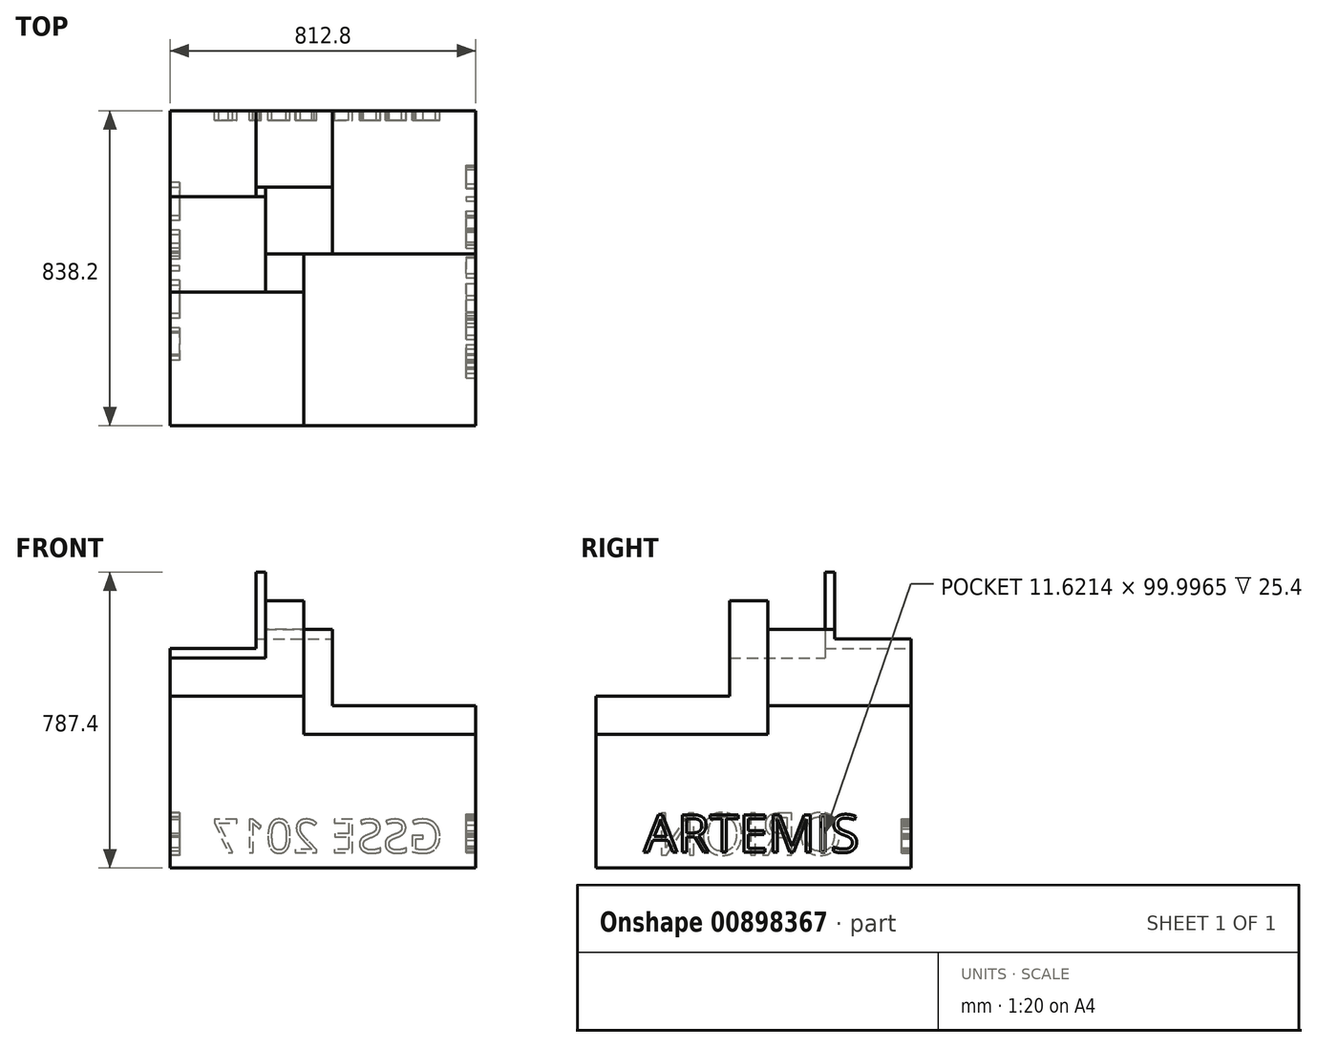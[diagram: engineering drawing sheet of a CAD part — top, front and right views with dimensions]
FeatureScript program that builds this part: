
annotation { "Feature Type Name" : "Feature", "Feature Type Description" : "" }
export const myFeature = defineFeature(function(context is Context, id is Id, definition is map)
    precondition{}
    {
        {
            var Q0;
            Q0=qCreatedBy(makeId("Top.planeOp"),FACE);
            var sketch = newSketch(context, id + "F0", { "sketchPlane" : qUnion([Q0])});
            skLineSegment(sketch, "E0.bottom", {"start": v(-76.2, -68.1) * mm, "end": v(381, -68.1) * mm});
            skLineSegment(sketch, "E0.top", {"start": v(-76.2, -525.3) * mm, "end": v(381, -525.3) * mm});
            skLineSegment(sketch, "E0.left", {"start": v(-76.2, -68.1) * mm, "end": v(-76.2, -525.3) * mm});
            skLineSegment(sketch, "E0.right", {"start": v(381, -68.1) * mm, "end": v(381, -525.3) * mm});
            skLineSegment(sketch, "E1.bottom", {"start": v(-76.2, -525.3) * mm, "end": v(-431.8, -525.3) * mm});
            skLineSegment(sketch, "E1.top", {"start": v(-76.2, -169.7) * mm, "end": v(-431.8, -169.7) * mm});
            skLineSegment(sketch, "E1.left", {"start": v(-76.2, -525.3) * mm, "end": v(-76.2, -169.7) * mm});
            skLineSegment(sketch, "E1.right", {"start": v(-431.8, -525.3) * mm, "end": v(-431.8, -169.7) * mm});
            skLineSegment(sketch, "E2.bottom", {"start": v(-76.2, -169.7) * mm, "end": v(-177.8, -169.7) * mm});
            skLineSegment(sketch, "E2.top", {"start": v(-76.2, -68.1) * mm, "end": v(-177.8, -68.1) * mm});
            skLineSegment(sketch, "E2.left", {"start": v(-76.2, -169.7) * mm, "end": v(-76.2, -68.1) * mm});
            skLineSegment(sketch, "E2.right", {"start": v(-177.8, -169.7) * mm, "end": v(-177.8, -68.1) * mm});
            skLineSegment(sketch, "E3.bottom", {"start": v(-431.8, -169.7) * mm, "end": v(-177.8, -169.7) * mm});
            skLineSegment(sketch, "E3.top", {"start": v(-431.8, 84.3) * mm, "end": v(-177.8, 84.3) * mm});
            skLineSegment(sketch, "E3.left", {"start": v(-431.8, -169.7) * mm, "end": v(-431.8, 84.3) * mm});
            skLineSegment(sketch, "E3.right", {"start": v(-177.8, -169.7) * mm, "end": v(-177.8, 84.3) * mm});
            skLineSegment(sketch, "E4.bottom", {"start": v(-431.8, 84.3) * mm, "end": v(-203.2, 84.3) * mm});
            skLineSegment(sketch, "E4.top", {"start": v(-431.8, 312.9) * mm, "end": v(-203.2, 312.9) * mm});
            skLineSegment(sketch, "E4.left", {"start": v(-431.8, 84.3) * mm, "end": v(-431.8, 312.9) * mm});
            skLineSegment(sketch, "E4.right", {"start": v(-203.2, 84.3) * mm, "end": v(-203.2, 312.9) * mm});
            skLineSegment(sketch, "E5.bottom", {"start": v(381, -68.1) * mm, "end": v(0, -68.1) * mm});
            skLineSegment(sketch, "E5.top", {"start": v(381, 312.9) * mm, "end": v(0, 312.9) * mm});
            skLineSegment(sketch, "E5.left", {"start": v(381, -68.1) * mm, "end": v(381, 312.9) * mm});
            skLineSegment(sketch, "E5.right", {"start": v(0, -68.1) * mm, "end": v(0, 312.9) * mm});
            skLineSegment(sketch, "E6.bottom", {"start": v(-203.2, 312.9) * mm, "end": v(0, 312.9) * mm});
            skLineSegment(sketch, "E6.top", {"start": v(-203.2, 109.7) * mm, "end": v(0, 109.7) * mm});
            skLineSegment(sketch, "E6.left", {"start": v(-203.2, 312.9) * mm, "end": v(-203.2, 109.7) * mm});
            skLineSegment(sketch, "E6.right", {"start": v(0, 312.9) * mm, "end": v(0, 109.7) * mm});
            skLineSegment(sketch, "E7.bottom", {"start": v(0, -68.1) * mm, "end": v(-177.8, -68.1) * mm});
            skLineSegment(sketch, "E7.top", {"start": v(0, 109.7) * mm, "end": v(-177.8, 109.7) * mm});
            skLineSegment(sketch, "E7.left", {"start": v(0, -68.1) * mm, "end": v(0, 109.7) * mm});
            skLineSegment(sketch, "E7.right", {"start": v(-177.8, -68.1) * mm, "end": v(-177.8, 109.7) * mm});
            skSolve(sketch);
        }
        {
            var Q0;
            {var subQ0=sQuery(id+"F0.wireOp",EDGE,"E7.right");Q0=makeQuery(id+"F0.imprint","IMPRINT",FACE,{"disambiguationData":[TD([[makeQuery(id+"F0.imprint","IMPRINT",EDGE,{"derivedFrom":subQ0}),1.0]])]});}
            extrude(context, id + "F1", {"entities" : qUnion([Q0]), "depth" : 787.4 * mm, "offsetDistance" : 25.4 * mm});
        }
        {
            var Q0;
            {var subQ1=sQuery(id+"F0.wireOp",EDGE,"E4.top");Q0=makeQuery(id+"F0.imprint","IMPRINT",FACE,{"disambiguationData":[TD([[makeQuery(id+"F0.imprint","IMPRINT",EDGE,{"derivedFrom":subQ1}),-1.0]])]});}
            extrude(context, id + "F2", {"entities" : qUnion([Q0]), "operationType" : NewBodyOperationType.ADD, "depth" : 584.2 * mm, "offsetDistance" : 25.4 * mm});
        }
        {
            var Q0;
            {var subQ4=sQuery(id+"F0.wireOp",EDGE,"E6.bottom");Q0=makeQuery(id+"F0.imprint","IMPRINT",FACE,{"disambiguationData":[TD([[makeQuery(id+"F0.imprint","IMPRINT",EDGE,{"derivedFrom":subQ4}),-1.0]])]});}
            extrude(context, id + "F3", {"entities" : qUnion([Q0]), "operationType" : NewBodyOperationType.ADD, "depth" : 609.6 * mm, "offsetDistance" : 25.4 * mm});
        }
        {
            var Q0;
            {var subQ1=sQuery(id+"F0.wireOp",EDGE,"E5.top");Q0=makeQuery(id+"F0.imprint","IMPRINT",FACE,{"disambiguationData":[TD([[makeQuery(id+"F0.imprint","IMPRINT",EDGE,{"derivedFrom":subQ1}),1.0]])]});}
            extrude(context, id + "F4", {"entities" : qUnion([Q0]), "operationType" : NewBodyOperationType.ADD, "depth" : 431.8 * mm, "offsetDistance" : 25.4 * mm});
        }
        {
            var Q0;
            {var subQ5=sQuery(id+"F0.wireOp",EDGE,"E2.top");Q0=makeQuery(id+"F0.imprint","IMPRINT",FACE,{"disambiguationData":[TD([[makeQuery(id+"F0.imprint","IMPRINT",EDGE,{"derivedFrom":subQ5}),-1.0]])]});}
            extrude(context, id + "F5", {"entities" : qUnion([Q0]), "operationType" : NewBodyOperationType.ADD, "depth" : 635 * mm, "offsetDistance" : 25.4 * mm});
        }
        {
            var Q0;
            {var subQ3=sQuery(id+"F0.wireOp",EDGE,"E2.right");Q0=makeQuery(id+"F0.imprint","IMPRINT",FACE,{"disambiguationData":[TD([[makeQuery(id+"F0.imprint","IMPRINT",EDGE,{"derivedFrom":subQ3}),1.0]])]});}
            extrude(context, id + "F6", {"entities" : qUnion([Q0]), "operationType" : NewBodyOperationType.ADD, "depth" : 558.8 * mm, "offsetDistance" : 25.4 * mm});
        }
        {
            var Q0;
            {var subQ3=sQuery(id+"F0.wireOp",EDGE,"E2.top");Q0=makeQuery(id+"F0.imprint","IMPRINT",FACE,{"disambiguationData":[TD([[makeQuery(id+"F0.imprint","IMPRINT",EDGE,{"derivedFrom":subQ3}),1.0]])]});}
            extrude(context, id + "F7", {"entities" : qUnion([Q0]), "operationType" : NewBodyOperationType.ADD, "depth" : 711.2 * mm, "offsetDistance" : 25.4 * mm});
        }
        {
            var Q0;
            {var subQ3=sQuery(id+"F0.wireOp",EDGE,"E1.bottom");Q0=makeQuery(id+"F0.imprint","IMPRINT",FACE,{"disambiguationData":[TD([[makeQuery(id+"F0.imprint","IMPRINT",EDGE,{"derivedFrom":subQ3}),-1.0]])]});}
            extrude(context, id + "F8", {"entities" : qUnion([Q0]), "operationType" : NewBodyOperationType.ADD, "depth" : 457.2 * mm, "offsetDistance" : 25.4 * mm});
        }
        {
            var Q0;
            {var subQ1=sQuery(id+"F0.wireOp",EDGE,"E0.top");Q0=makeQuery(id+"F0.imprint","IMPRINT",FACE,{"disambiguationData":[TD([[makeQuery(id+"F0.imprint","IMPRINT",EDGE,{"derivedFrom":subQ1}),1.0]])]});}
            extrude(context, id + "F9", {"entities" : qUnion([Q0]), "operationType" : NewBodyOperationType.ADD, "depth" : 355.6 * mm, "offsetDistance" : 25.4 * mm});
        }
        {
            var Q0;
            Q0=makeQuery(id+"F4.boolean.opBoolean","MERGE",FACE,{"derivedFrom":[makeQuery(id+"F3.boolean.opBoolean","MERGE",FACE,{"derivedFrom":[makeQuery(id+"F2.opExtrude","SWEPT_FACE",FACE,{"disambiguationData":[OSD([sQuery(id+"F0.wireOp",EDGE,"E4.top")])]}),makeQuery(id+"F3.opExtrude","SWEPT_FACE",FACE,{"disambiguationData":[OSD([sQuery(id+"F0.wireOp",EDGE,"E6.bottom")])]})]}),makeQuery(id+"F4.opExtrude","SWEPT_FACE",FACE,{"disambiguationData":[OSD([sQuery(id+"F0.wireOp",EDGE,"E5.top")])]})]});
            var sketch = newSketch(context, id + "F10", { "sketchPlane" : qUnion([Q0])});
            skText(sketch, "E8", { "text": "GSSE 2017\n", "fontName": "OpenSans-Regular.ttf"});
            const initialGuessF10  = {"E8": [-0.29332, 0.0403, 1, 0, 0.0895]};
            skSetInitialGuess(sketch, initialGuessF10);
            skSolve(sketch);
        }
        {
            var Q0;
            Q0=qSketchRegion(id+"F10",true);
            extrude(context, id + "F11", {"entities" : qUnion([Q0]), "operationType" : NewBodyOperationType.REMOVE, "oppositeDirection" : true, "depth" : 25.4 * mm, "offsetDistance" : 25.4 * mm});
        }
        {
            var Q0;
            Q0=makeQuery(id+"F8.boolean.opBoolean","MERGE",FACE,{"derivedFrom":[makeQuery(id+"F6.boolean.opBoolean","MERGE",FACE,{"derivedFrom":[makeQuery(id+"F2.opExtrude","SWEPT_FACE",FACE,{"disambiguationData":[OSD([sQuery(id+"F0.wireOp",EDGE,"E4.left")])]}),makeQuery(id+"F6.opExtrude","SWEPT_FACE",FACE,{"disambiguationData":[OSD([sQuery(id+"F0.wireOp",EDGE,"E3.left")])]})]}),makeQuery(id+"F8.opExtrude","SWEPT_FACE",FACE,{"disambiguationData":[OSD([sQuery(id+"F0.wireOp",EDGE,"E1.right")])]})]});
            var sketch = newSketch(context, id + "F12", { "sketchPlane" : qUnion([Q0])});
            skText(sketch, "E9", { "text": "ORION", "fontName": "OpenSans-Regular.ttf"});
            const initialGuessF12  = {"E9": [-0.132, 0.03486, 1, 0, 0.11188]};
            skSetInitialGuess(sketch, initialGuessF12);
            skSolve(sketch);
        }
        {
            var Q0;
            Q0=qSketchRegion(id+"F12",true);
            extrude(context, id + "F13", {"entities" : qUnion([Q0]), "operationType" : NewBodyOperationType.REMOVE, "oppositeDirection" : true, "depth" : 25.4 * mm, "offsetDistance" : 25.4 * mm});
        }
        {
            var Q0;
            Q0=makeQuery(id+"F9.boolean.opBoolean","MERGE",FACE,{"derivedFrom":[makeQuery(id+"F4.opExtrude","SWEPT_FACE",FACE,{"disambiguationData":[OSD([sQuery(id+"F0.wireOp",EDGE,"E5.left")])]}),makeQuery(id+"F9.opExtrude","SWEPT_FACE",FACE,{"disambiguationData":[OSD([sQuery(id+"F0.wireOp",EDGE,"E0.right")])]})]});
            var sketch = newSketch(context, id + "F14", { "sketchPlane" : qUnion([Q0])});
            skText(sketch, "E10", { "text": "ARTEMIS", "fontName": "OpenSans-Regular.ttf"});
            const initialGuessF14  = {"E10": [-0.3977, 0.04163, 1, 0, 0.10085]};
            skSetInitialGuess(sketch, initialGuessF14);
            skSolve(sketch);
        }
        {
            var Q0;
            Q0=qSketchRegion(id+"F14",true);
            extrude(context, id + "F15", {"entities" : qUnion([Q0]), "operationType" : NewBodyOperationType.REMOVE, "oppositeDirection" : true, "depth" : 25.4 * mm, "offsetDistance" : 25.4 * mm});
        }
    });
